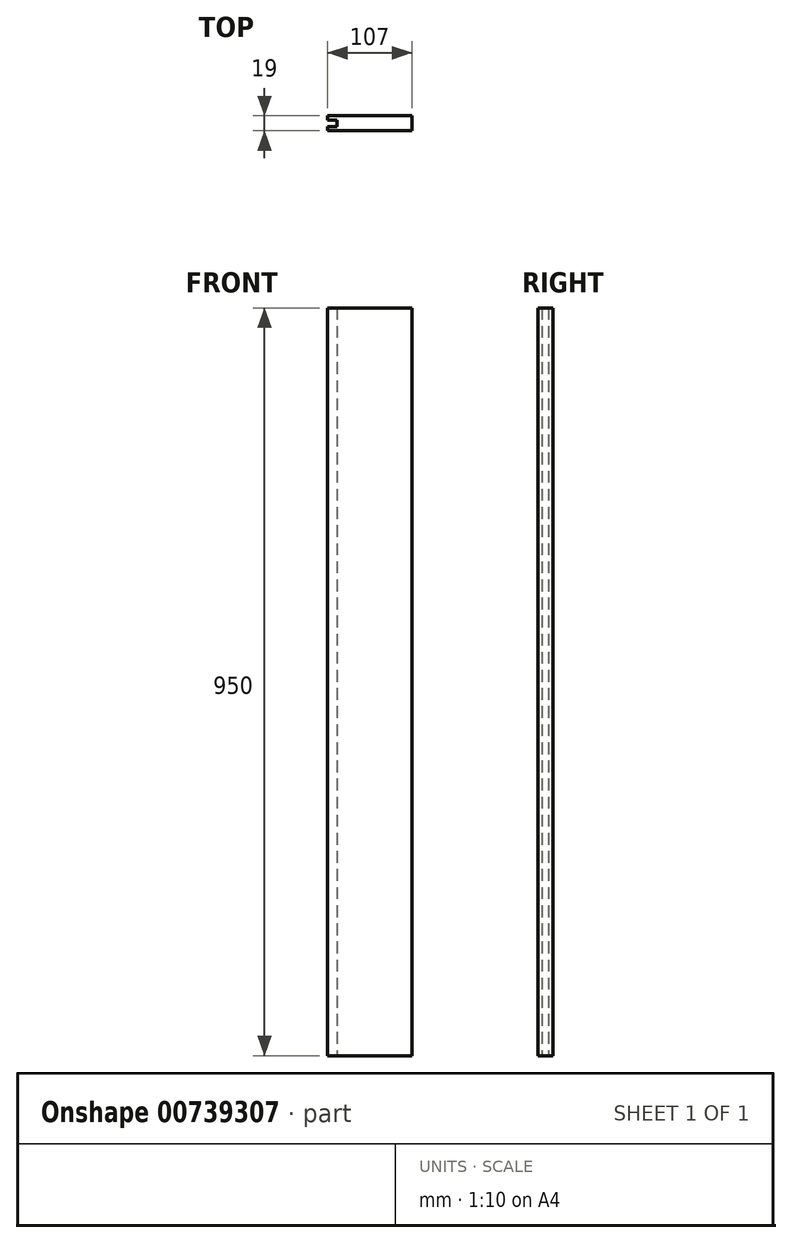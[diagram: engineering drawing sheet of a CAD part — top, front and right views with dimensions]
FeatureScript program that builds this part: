
annotation { "Feature Type Name" : "Feature", "Feature Type Description" : "" }
export const myFeature = defineFeature(function(context is Context, id is Id, definition is map)
    precondition{}
    {
        {
            var Q0;
            Q0=qCreatedBy(makeId("Top.planeOp"),FACE);
            var sketch = newSketch(context, id + "F0", { "sketchPlane" : qUnion([Q0])});
            skLineSegment(sketch, "E0.bottom", {"start": v(0, -9.5) * mm, "end": v(136, -9.5) * mm});
            skLineSegment(sketch, "E0.top", {"start": v(0, 9.5) * mm, "end": v(110.5, 9.5) * mm});
            skLineSegment(sketch, "E0.left", {"start": v(0, -9.5) * mm, "end": v(0, -4) * mm});
            skLineSegment(sketch, "E0.right", {"start": v(136, -9.5) * mm, "end": v(136, -4) * mm});
            skLineSegment(sketch, "E1", {"start": v(0, -4) * mm, "end": v(12, -4) * mm});
            skLineSegment(sketch, "E2", {"start": v(12, -4) * mm, "end": v(12, 4) * mm});
            skLineSegment(sketch, "E3", {"start": v(12, 4) * mm, "end": v(0, 4) * mm});
            skLineSegment(sketch, "E4.trimOffspring", {"start": v(0, 4) * mm, "end": v(0, 9.5) * mm});
            skLineSegment(sketch, "E5", {"start": v(136, -4) * mm, "end": v(146, -4) * mm});
            skLineSegment(sketch, "E6", {"start": v(146, -4) * mm, "end": v(146, 4) * mm});
            skLineSegment(sketch, "E7", {"start": v(146, 4) * mm, "end": v(116, 4) * mm});
            skLineSegment(sketch, "E8.trimOffspring", {"start": v(116, 4) * mm, "end": v(110.5, 9.5) * mm});
            skSolve(sketch);
        }
        {
            var Q0;
            Q0=makeQuery(id+"F0.imprint","IMPRINT",FACE,{"disambiguationData":[TD([[makeQuery(id+"F0.imprint","IMPRINT",EDGE,{"derivedFrom":sQuery(id+"F0.wireOp",EDGE,"E0.bottom")}),1.0]])]});
            extrude(context, id + "F1", {"entities" : qUnion([Q0]), "depth" : 950 * mm, "offsetDistance" : 25 * mm});
        }
        {
            var Q0;
            Q0=makeQuery(id+"F1.opExtrude","CAP_FACE",FACE,{"disambiguationData":[OSD([sQuery(id+"F0.wireOp",EDGE,"E0.bottom"),sQuery(id+"F0.wireOp",EDGE,"E0.top"),sQuery(id+"F0.wireOp",EDGE,"E0.left"),sQuery(id+"F0.wireOp",EDGE,"E0.right"),sQuery(id+"F0.wireOp",EDGE,"E1"),sQuery(id+"F0.wireOp",EDGE,"E2"),sQuery(id+"F0.wireOp",EDGE,"E3"),sQuery(id+"F0.wireOp",EDGE,"E4.trimOffspring"),sQuery(id+"F0.wireOp",EDGE,"E5"),sQuery(id+"F0.wireOp",EDGE,"E6"),sQuery(id+"F0.wireOp",EDGE,"E7"),sQuery(id+"F0.wireOp",EDGE,"E8.trimOffspring")])],"isStart":true});
            var sketch = newSketch(context, id + "F2", { "sketchPlane" : qUnion([Q0])});
            skLineSegment(sketch, "E9", {"start": v(107, -9.5) * mm, "end": v(107, 9.5) * mm});
            skSolve(sketch);
        }
        {
            var Q0;
            {var subQ1=sQuery(id+"F2.wireOp",EDGE,"E9");Q0=makeQuery(id+"F2.imprint","IMPRINT",FACE,{"disambiguationData":[TD([[makeQuery(id+"F2.imprint","IMPRINT",EDGE,{"derivedFrom":subQ1}),-1.0]])]});}
            extrude(context, id + "F3", {"entities" : qUnion([Q0]), "operationType" : NewBodyOperationType.REMOVE, "endBound" : BoundingType.THROUGH_ALL, "oppositeDirection" : true, "depth" : 25 * mm, "offsetDistance" : 25 * mm});
        }
    });
